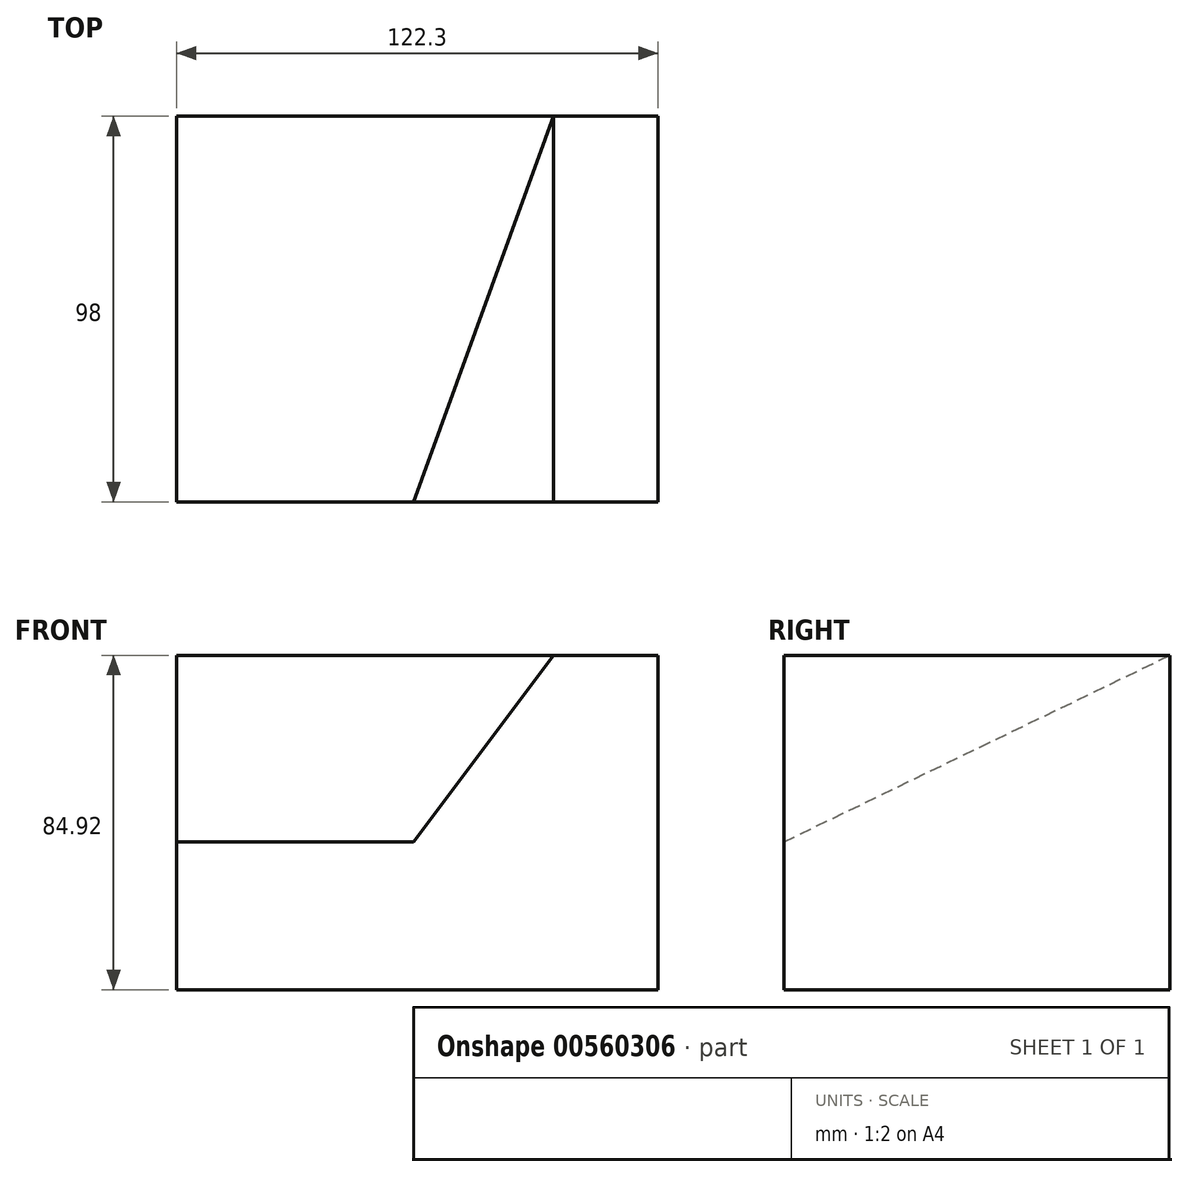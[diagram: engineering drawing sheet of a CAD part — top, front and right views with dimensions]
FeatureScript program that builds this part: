
annotation { "Feature Type Name" : "Feature", "Feature Type Description" : "" }
export const myFeature = defineFeature(function(context is Context, id is Id, definition is map)
    precondition{}
    {
        {
            var Q0;
            Q0=qCreatedBy(makeId("Front.planeOp"),FACE);
            var sketch = newSketch(context, id + "F0", { "sketchPlane" : qUnion([Q0])});
            skLineSegment(sketch, "E0", {"start": v(0, 0) * mm, "end": v(35.56, 47.36) * mm});
            skLineSegment(sketch, "E1", {"start": v(35.56, 47.36) * mm, "end": v(62.06, 47.36) * mm});
            skLineSegment(sketch, "E2", {"start": v(62.06, 47.36) * mm, "end": v(62.06, -37.56) * mm});
            skLineSegment(sketch, "E3", {"start": v(62.06, -37.56) * mm, "end": v(-60.24, -37.56) * mm});
            skLineSegment(sketch, "E4", {"start": v(-60.24, -37.56) * mm, "end": v(-60.24, 0) * mm});
            skLineSegment(sketch, "E5", {"start": v(-60.24, 0) * mm, "end": v(0, 0) * mm});
            skSolve(sketch);
        }
        {
            var Q0;
            Q0=makeQuery(id+"F0.imprint","IMPRINT",FACE,{"disambiguationData":[TD([[makeQuery(id+"F0.imprint","IMPRINT",EDGE,{"derivedFrom":sQuery(id+"F0.wireOp",EDGE,"E0")}),-1.0]])]});
            extrude(context, id + "F1", {"entities" : qUnion([Q0]), "endBound" : BoundingType.SYMMETRIC, "depth" : 98 * mm, "offsetDistance" : 25 * mm});
        }
        {
            var Q0;
            Q0=makeQuery(id+"F1.opExtrude","SWEPT_FACE",FACE,{"disambiguationData":[OSD([sQuery(id+"F0.wireOp",EDGE,"E4")])]});
            var sketch = newSketch(context, id + "F2", { "sketchPlane" : qUnion([Q0])});
            skLineSegment(sketch, "E6.0", {"start": v(49, 47.36) * mm, "end": v(-49, 47.36) * mm, "construction": true});
            skLineSegment(sketch, "E7.0", {"start": v(-49, 0) * mm, "end": v(-49, 47.36) * mm});
            skLineSegment(sketch, "E8", {"start": v(-49, 47.36) * mm, "end": v(49, 0) * mm});
            skLineSegment(sketch, "E9", {"start": v(49, 0) * mm, "end": v(-49, 0) * mm});
            skSolve(sketch);
        }
        {
            var Q0;
            Q0=makeQuery(id+"F2.imprint","IMPRINT",FACE,{"disambiguationData":[TD([[makeQuery(id+"F2.imprint","IMPRINT",EDGE,{"derivedFrom":sQuery(id+"F2.wireOp",EDGE,"E7.0")}),-1.0]])]});
            var Q1;
            Q1=makeQuery(id+"F1.opExtrude","SWEPT_FACE",FACE,{"disambiguationData":[OSD([sQuery(id+"F0.wireOp",EDGE,"E0")])]});
            extrude(context, id + "F3", {"entities" : qUnion([Q0]), "operationType" : NewBodyOperationType.ADD, "endBound" : BoundingType.UP_TO_SURFACE, "oppositeDirection" : true, "depth" : 25 * mm, "endBoundEntityFace" : qUnion([Q1]), "offsetDistance" : 25 * mm});
        }
    });
